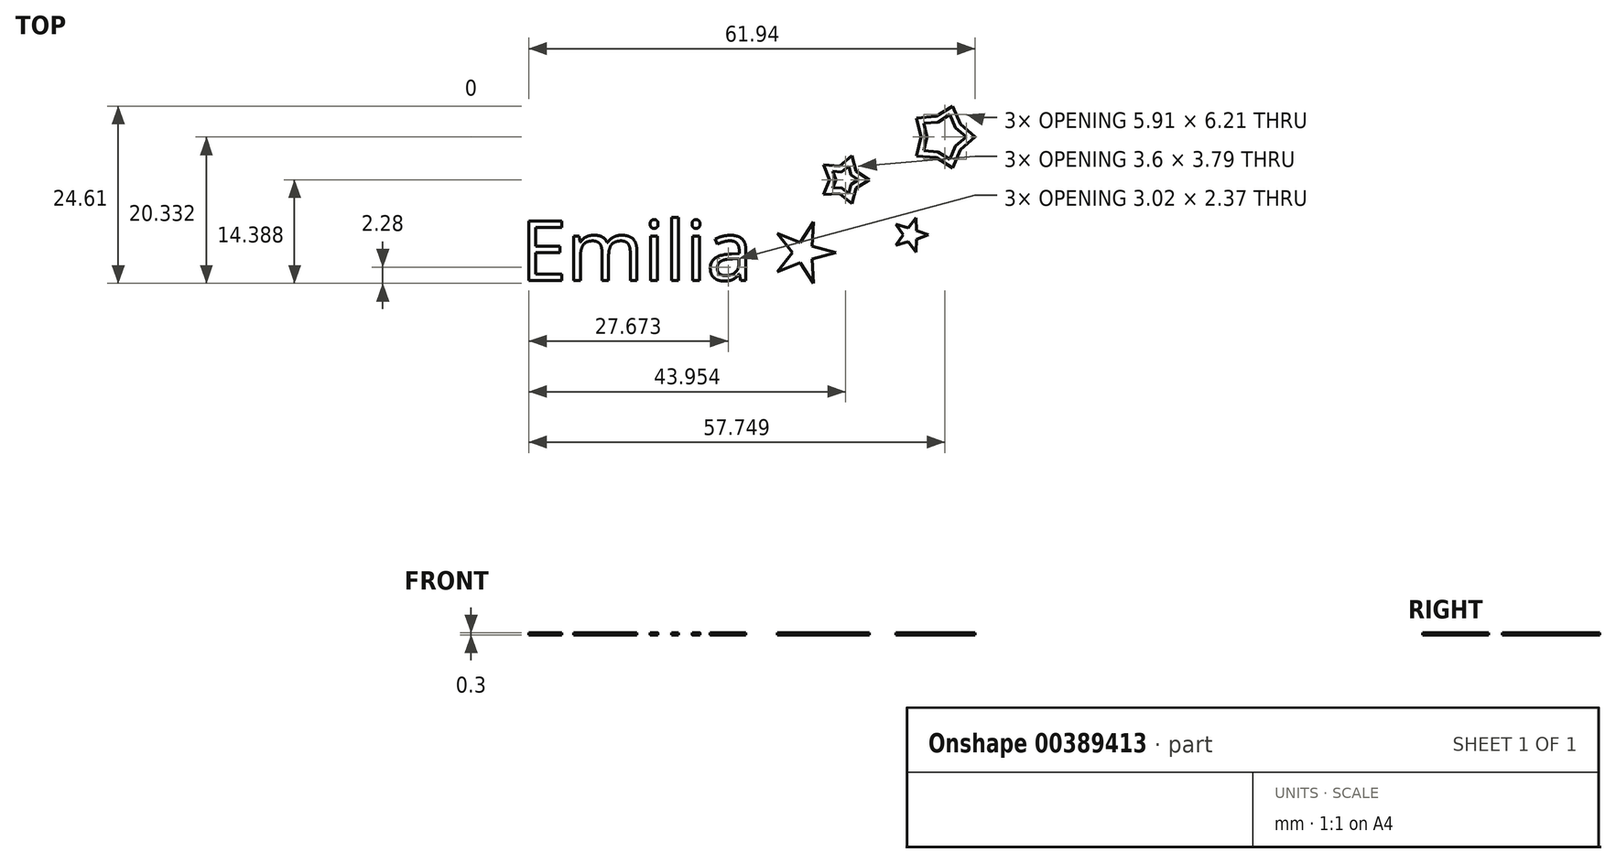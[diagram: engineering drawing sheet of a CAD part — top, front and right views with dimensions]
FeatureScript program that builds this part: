
annotation { "Feature Type Name" : "Feature", "Feature Type Description" : "" }
export const myFeature = defineFeature(function(context is Context, id is Id, definition is map)
    precondition{}
    {
        {
            var Q0;
            Q0=qCreatedBy(makeId("Top.planeOp"),FACE);
            var sketch = newSketch(context, id + "F0", { "sketchPlane" : qUnion([Q0])});
            skCircle(sketch, "E0.cCircle", {"center": v(46.45, 16.36) * mm, "radius": 4.5 * mm, "construction": true});
            skLineSegment(sketch, "E0.0", {"start": v(50.95, 16.36) * mm, "end": v(47.84, 12.08) * mm, "construction": true});
            skLineSegment(sketch, "E0.1", {"start": v(47.84, 12.08) * mm, "end": v(42.8, 13.72) * mm, "construction": true});
            skLineSegment(sketch, "E0.2", {"start": v(42.8, 13.72) * mm, "end": v(42.8, 19) * mm, "construction": true});
            skLineSegment(sketch, "E0.3", {"start": v(42.8, 19) * mm, "end": v(47.84, 20.64) * mm, "construction": true});
            skLineSegment(sketch, "E0.4", {"start": v(47.84, 20.64) * mm, "end": v(50.95, 16.36) * mm, "construction": true});
            skCircle(sketch, "E1.cCircle", {"center": v(46.45, 16.36) * mm, "radius": 3 * mm, "construction": true});
            skLineSegment(sketch, "E1.0", {"start": v(48.87, 18.13) * mm, "end": v(48.87, 14.6) * mm, "construction": true});
            skLineSegment(sketch, "E1.1", {"start": v(48.87, 14.6) * mm, "end": v(45.52, 13.5) * mm, "construction": true});
            skLineSegment(sketch, "E1.2", {"start": v(45.52, 13.5) * mm, "end": v(43.45, 16.36) * mm, "construction": true});
            skLineSegment(sketch, "E1.3", {"start": v(43.45, 16.36) * mm, "end": v(45.52, 19.21) * mm, "construction": true});
            skLineSegment(sketch, "E1.4", {"start": v(45.52, 19.21) * mm, "end": v(48.87, 18.13) * mm, "construction": true});
            skLineSegment(sketch, "E2", {"start": v(42.8, 19) * mm, "end": v(43.45, 16.36) * mm});
            skLineSegment(sketch, "E3", {"start": v(42.8, 13.72) * mm, "end": v(43.45, 16.36) * mm});
            skLineSegment(sketch, "E4", {"start": v(42.8, 13.72) * mm, "end": v(45.52, 13.5) * mm});
            skLineSegment(sketch, "E5", {"start": v(45.52, 13.5) * mm, "end": v(47.84, 12.08) * mm});
            skLineSegment(sketch, "E6", {"start": v(47.84, 12.08) * mm, "end": v(48.87, 14.6) * mm});
            skLineSegment(sketch, "E7", {"start": v(48.87, 14.6) * mm, "end": v(50.95, 16.36) * mm});
            skLineSegment(sketch, "E8", {"start": v(50.95, 16.36) * mm, "end": v(48.87, 18.13) * mm});
            skLineSegment(sketch, "E9", {"start": v(48.87, 18.13) * mm, "end": v(47.84, 20.64) * mm});
            skLineSegment(sketch, "E10", {"start": v(47.84, 20.64) * mm, "end": v(45.52, 19.21) * mm});
            skLineSegment(sketch, "E11", {"start": v(45.52, 19.21) * mm, "end": v(42.8, 19) * mm});
            skCircle(sketch, "E12.cCircle", {"center": v(32.77, 10.42) * mm, "radius": 3.5 * mm, "construction": true});
            skLineSegment(sketch, "E12.0", {"start": v(36.27, 10.42) * mm, "end": v(33.86, 7.09) * mm, "construction": true});
            skLineSegment(sketch, "E12.1", {"start": v(33.86, 7.09) * mm, "end": v(29.94, 8.36) * mm, "construction": true});
            skLineSegment(sketch, "E12.2", {"start": v(29.94, 8.36) * mm, "end": v(29.94, 12.47) * mm, "construction": true});
            skLineSegment(sketch, "E12.3", {"start": v(29.94, 12.47) * mm, "end": v(33.86, 13.75) * mm, "construction": true});
            skLineSegment(sketch, "E12.4", {"start": v(33.86, 13.75) * mm, "end": v(36.27, 10.42) * mm, "construction": true});
            skCircle(sketch, "E13.cCircle", {"center": v(32.77, 10.42) * mm, "radius": 2 * mm, "construction": true});
            skLineSegment(sketch, "E13.0", {"start": v(34.4, 11.6) * mm, "end": v(34.4, 9.24) * mm, "construction": true});
            skLineSegment(sketch, "E13.1", {"start": v(34.4, 9.24) * mm, "end": v(32.16, 8.52) * mm, "construction": true});
            skLineSegment(sketch, "E13.2", {"start": v(32.16, 8.52) * mm, "end": v(30.77, 10.42) * mm, "construction": true});
            skLineSegment(sketch, "E13.3", {"start": v(30.77, 10.42) * mm, "end": v(32.16, 12.32) * mm, "construction": true});
            skLineSegment(sketch, "E13.4", {"start": v(32.16, 12.32) * mm, "end": v(34.4, 11.6) * mm, "construction": true});
            skLineSegment(sketch, "E14", {"start": v(29.94, 12.47) * mm, "end": v(30.77, 10.42) * mm});
            skLineSegment(sketch, "E15", {"start": v(29.94, 8.36) * mm, "end": v(30.77, 10.42) * mm});
            skLineSegment(sketch, "E16", {"start": v(29.94, 8.36) * mm, "end": v(32.16, 8.52) * mm});
            skLineSegment(sketch, "E17", {"start": v(32.16, 8.52) * mm, "end": v(33.86, 7.09) * mm});
            skLineSegment(sketch, "E18", {"start": v(33.86, 7.09) * mm, "end": v(34.4, 9.24) * mm});
            skLineSegment(sketch, "E19", {"start": v(34.4, 9.24) * mm, "end": v(36.27, 10.42) * mm});
            skLineSegment(sketch, "E20", {"start": v(36.27, 10.42) * mm, "end": v(34.4, 11.6) * mm});
            skLineSegment(sketch, "E21", {"start": v(34.4, 11.6) * mm, "end": v(33.86, 13.75) * mm});
            skLineSegment(sketch, "E22", {"start": v(33.86, 13.75) * mm, "end": v(32.16, 12.32) * mm});
            skLineSegment(sketch, "E23", {"start": v(32.16, 12.32) * mm, "end": v(29.94, 12.47) * mm});
            skCircle(sketch, "E24.cCircle", {"center": v(41.99, 2.77) * mm, "radius": 2.5 * mm, "construction": true});
            skLineSegment(sketch, "E24.0", {"start": v(44.49, 2.77) * mm, "end": v(42.76, 0.39) * mm, "construction": true});
            skLineSegment(sketch, "E24.1", {"start": v(42.76, 0.39) * mm, "end": v(39.97, 1.3) * mm, "construction": true});
            skLineSegment(sketch, "E24.2", {"start": v(39.97, 1.3) * mm, "end": v(39.97, 4.24) * mm, "construction": true});
            skLineSegment(sketch, "E24.3", {"start": v(39.97, 4.24) * mm, "end": v(42.76, 5.14) * mm, "construction": true});
            skLineSegment(sketch, "E24.4", {"start": v(42.76, 5.14) * mm, "end": v(44.49, 2.77) * mm, "construction": true});
            skCircle(sketch, "E25.cCircle", {"center": v(41.99, 2.77) * mm, "radius": 1 * mm, "construction": true});
            skLineSegment(sketch, "E25.0", {"start": v(42.8, 3.36) * mm, "end": v(42.8, 2.18) * mm, "construction": true});
            skLineSegment(sketch, "E25.1", {"start": v(42.8, 2.18) * mm, "end": v(41.68, 1.82) * mm, "construction": true});
            skLineSegment(sketch, "E25.2", {"start": v(41.68, 1.82) * mm, "end": v(40.99, 2.77) * mm, "construction": true});
            skLineSegment(sketch, "E25.3", {"start": v(40.99, 2.77) * mm, "end": v(41.68, 3.72) * mm, "construction": true});
            skLineSegment(sketch, "E25.4", {"start": v(41.68, 3.72) * mm, "end": v(42.8, 3.36) * mm, "construction": true});
            skLineSegment(sketch, "E26", {"start": v(39.97, 4.24) * mm, "end": v(40.99, 2.77) * mm});
            skLineSegment(sketch, "E27", {"start": v(39.97, 1.3) * mm, "end": v(40.99, 2.77) * mm});
            skLineSegment(sketch, "E28", {"start": v(39.97, 1.3) * mm, "end": v(41.68, 1.82) * mm});
            skLineSegment(sketch, "E29", {"start": v(41.68, 1.82) * mm, "end": v(42.76, 0.39) * mm});
            skLineSegment(sketch, "E30", {"start": v(42.76, 0.39) * mm, "end": v(42.8, 2.18) * mm});
            skLineSegment(sketch, "E31", {"start": v(42.8, 2.18) * mm, "end": v(44.49, 2.77) * mm});
            skLineSegment(sketch, "E32", {"start": v(44.49, 2.77) * mm, "end": v(42.8, 3.36) * mm});
            skLineSegment(sketch, "E33", {"start": v(42.8, 3.36) * mm, "end": v(42.76, 5.14) * mm});
            skLineSegment(sketch, "E34", {"start": v(42.76, 5.14) * mm, "end": v(41.68, 3.72) * mm});
            skLineSegment(sketch, "E35", {"start": v(41.68, 3.72) * mm, "end": v(39.97, 4.24) * mm});
            skCircle(sketch, "E36.cCircle", {"center": v(27.11, 0.31) * mm, "radius": 4.5 * mm, "construction": true});
            skLineSegment(sketch, "E36.0", {"start": v(31.61, 0.31) * mm, "end": v(28.5, -3.97) * mm, "construction": true});
            skLineSegment(sketch, "E36.1", {"start": v(28.5, -3.97) * mm, "end": v(23.47, -2.33) * mm, "construction": true});
            skLineSegment(sketch, "E36.2", {"start": v(23.47, -2.33) * mm, "end": v(23.47, 2.96) * mm, "construction": true});
            skLineSegment(sketch, "E36.3", {"start": v(23.47, 2.96) * mm, "end": v(28.5, 4.6) * mm, "construction": true});
            skLineSegment(sketch, "E36.4", {"start": v(28.5, 4.6) * mm, "end": v(31.61, 0.31) * mm, "construction": true});
            skCircle(sketch, "E37.cCircle", {"center": v(27.11, 0.31) * mm, "radius": 1.5 * mm, "construction": true});
            skLineSegment(sketch, "E37.0", {"start": v(28.32, 1.2) * mm, "end": v(28.32, -0.57) * mm, "construction": true});
            skLineSegment(sketch, "E37.1", {"start": v(28.32, -0.57) * mm, "end": v(26.65, -1.11) * mm, "construction": true});
            skLineSegment(sketch, "E37.2", {"start": v(26.65, -1.11) * mm, "end": v(25.61, 0.31) * mm, "construction": true});
            skLineSegment(sketch, "E37.3", {"start": v(25.61, 0.31) * mm, "end": v(26.65, 1.74) * mm, "construction": true});
            skLineSegment(sketch, "E37.4", {"start": v(26.65, 1.74) * mm, "end": v(28.32, 1.2) * mm, "construction": true});
            skLineSegment(sketch, "E38", {"start": v(23.47, 2.96) * mm, "end": v(25.61, 0.31) * mm});
            skLineSegment(sketch, "E39", {"start": v(23.47, -2.33) * mm, "end": v(25.61, 0.31) * mm});
            skLineSegment(sketch, "E40", {"start": v(23.47, -2.33) * mm, "end": v(26.65, -1.11) * mm});
            skLineSegment(sketch, "E41", {"start": v(26.65, -1.11) * mm, "end": v(28.5, -3.97) * mm});
            skLineSegment(sketch, "E42", {"start": v(28.5, -3.97) * mm, "end": v(28.32, -0.57) * mm});
            skLineSegment(sketch, "E43", {"start": v(28.32, -0.57) * mm, "end": v(31.61, 0.31) * mm});
            skLineSegment(sketch, "E44", {"start": v(31.61, 0.31) * mm, "end": v(28.32, 1.2) * mm});
            skLineSegment(sketch, "E45", {"start": v(28.32, 1.2) * mm, "end": v(28.5, 4.6) * mm});
            skLineSegment(sketch, "E46", {"start": v(28.5, 4.6) * mm, "end": v(26.65, 1.74) * mm});
            skLineSegment(sketch, "E47", {"start": v(26.65, 1.74) * mm, "end": v(23.47, 2.96) * mm});
            skLineSegment(sketch, "E48.0", {"start": v(48.2, 17.64) * mm, "end": v(47.46, 19.47) * mm});
            skLineSegment(sketch, "E48.1", {"start": v(49.71, 16.36) * mm, "end": v(48.2, 17.64) * mm});
            skLineSegment(sketch, "E48.2", {"start": v(47.46, 19.47) * mm, "end": v(45.77, 18.43) * mm});
            skLineSegment(sketch, "E48.3", {"start": v(48.2, 15.08) * mm, "end": v(49.71, 16.36) * mm});
            skLineSegment(sketch, "E48.4", {"start": v(47.46, 13.26) * mm, "end": v(48.2, 15.08) * mm});
            skLineSegment(sketch, "E48.5", {"start": v(45.77, 14.3) * mm, "end": v(47.46, 13.26) * mm});
            skLineSegment(sketch, "E48.6", {"start": v(45.77, 18.43) * mm, "end": v(43.8, 18.28) * mm});
            skLineSegment(sketch, "E48.7", {"start": v(43.8, 18.28) * mm, "end": v(44.27, 16.36) * mm});
            skLineSegment(sketch, "E48.8", {"start": v(43.8, 14.44) * mm, "end": v(44.27, 16.36) * mm});
            skLineSegment(sketch, "E48.9", {"start": v(43.8, 14.44) * mm, "end": v(45.77, 14.3) * mm});
            skLineSegment(sketch, "E49.0", {"start": v(33.7, 11.09) * mm, "end": v(33.39, 12.31) * mm});
            skLineSegment(sketch, "E49.1", {"start": v(34.76, 10.42) * mm, "end": v(33.7, 11.09) * mm});
            skLineSegment(sketch, "E49.2", {"start": v(33.39, 12.31) * mm, "end": v(32.42, 11.5) * mm});
            skLineSegment(sketch, "E49.3", {"start": v(33.7, 9.75) * mm, "end": v(34.76, 10.42) * mm});
            skLineSegment(sketch, "E49.4", {"start": v(33.39, 8.53) * mm, "end": v(33.7, 9.75) * mm});
            skLineSegment(sketch, "E49.5", {"start": v(32.42, 9.34) * mm, "end": v(33.39, 8.53) * mm});
            skLineSegment(sketch, "E49.6", {"start": v(32.42, 11.5) * mm, "end": v(31.16, 11.59) * mm});
            skLineSegment(sketch, "E49.7", {"start": v(31.16, 11.59) * mm, "end": v(31.64, 10.42) * mm});
            skLineSegment(sketch, "E49.8", {"start": v(31.16, 9.25) * mm, "end": v(31.64, 10.42) * mm});
            skLineSegment(sketch, "E49.9", {"start": v(31.16, 9.25) * mm, "end": v(32.42, 9.34) * mm});
            skText(sketch, "E50", { "text": "Emilia", "fontName": "OpenSans-Regular.ttf"});
            const initialGuessF0  = {"E50": [-0.01212, -0.00353, 1, 0, 0.00827]};
            skSetInitialGuess(sketch, initialGuessF0);
            skSolve(sketch);
        }
        {
            var Q0;
            Q0=qSketchRegion(id+"F0",true);
            extrude(context, id + "F1", {"entities" : qUnion([Q0]), "depth" : 0.3 * mm});
        }
    });
